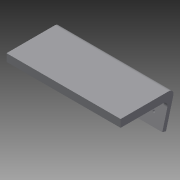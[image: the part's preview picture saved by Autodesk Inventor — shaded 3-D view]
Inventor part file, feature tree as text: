
AUTODESK INVENTOR PART (.ipt)
format: ipt  version: 2015 SP1 (Build 190203100, 203)  size: 143,872 bytes
history: native  units: mm
features: extrude x5, sketch x5, projected_geometry x4, other x1, fillet x1
ambient origin geometry x8: Origin, YZ Plane, XZ Plane, XY Plane, X Axis, Y Axis, Z Axis, Center Point
bodies: Body1 (feature_tree)
feature tree (16):
  other  "Sólido1"
  extrude  "Extrusión1"  Depth=150.0mm
  extrude  "Extrusión2"  Depth=5.0mm
  extrude  "Extrusión3"  Depth=5.0mm
  extrude  "Extrusión4"  Depth=5.0mm
  fillet  "Empalme1"  Radius=5.0mm
  extrude  "Extrusión5"  Depth=5.0mm
  sketch  "Boceto1"  dims[d0=150.0mm d1=70.0mm]
  sketch  "Boceto2"  dims[d2=5.0mm d3=0.0mm d4=40.0mm]
  projected_geometry  "Contorno proyectado1"
  sketch  "Boceto3"  dims[d5=15.0deg d6=5.0mm]
  projected_geometry  "Contorno proyectado2"
  sketch  "Boceto4"  dims[d7=5.0mm d8=0.0mm d9=5.0mm d10=5.0mm]
  projected_geometry  "Contorno proyectado3"
  sketch  "Boceto5"  dims[d11=5.0mm d12=0.0mm d14=5.0mm d15=5.0mm d16=5.0mm d17=5.0mm d18=0.0mm d19=6.0mm d20=15.0mm d21=15.0mm d22=180.0deg d23=3.0mm d24=100.0mm d25=3.0mm d26=5.0mm d27=0.0mm]
  projected_geometry  "Contorno proyectado4"
